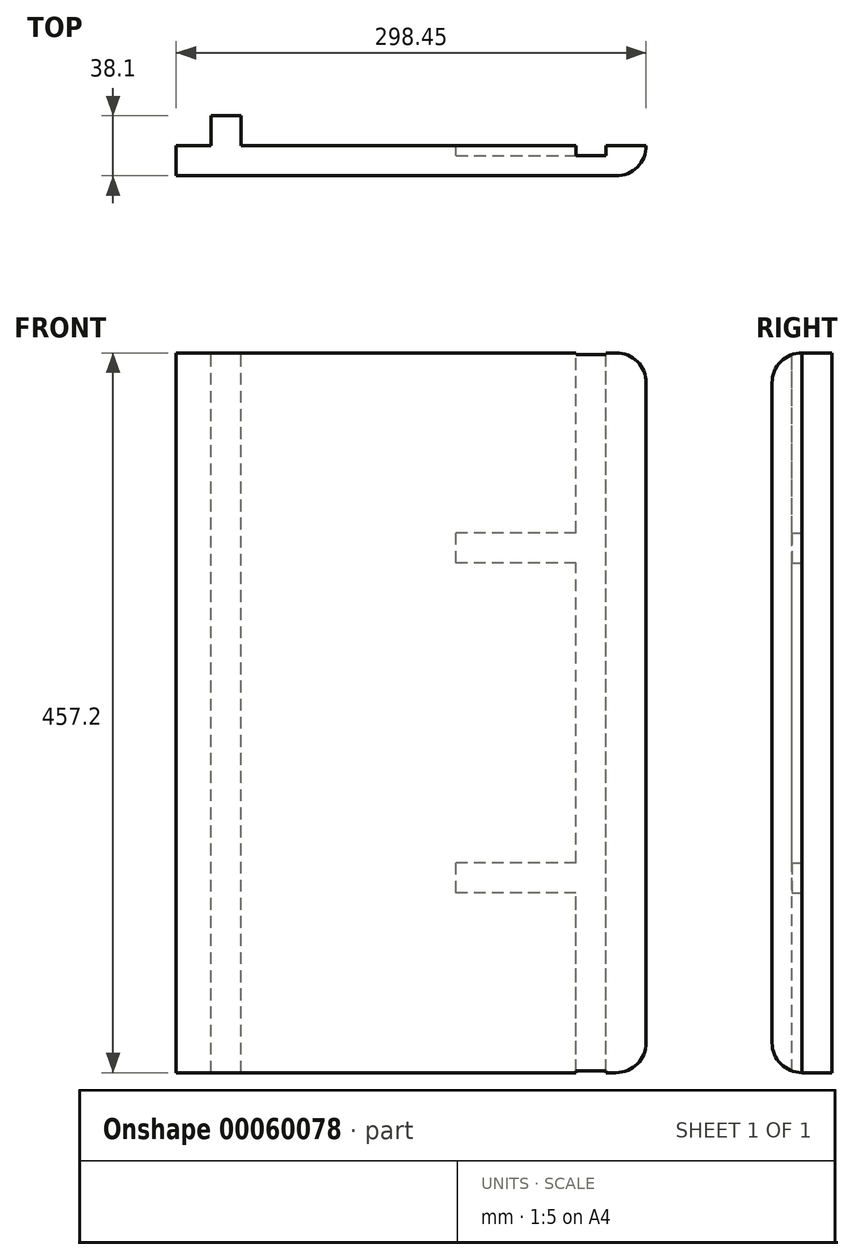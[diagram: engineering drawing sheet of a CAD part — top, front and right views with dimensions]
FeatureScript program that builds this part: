
annotation { "Feature Type Name" : "Feature", "Feature Type Description" : "" }
export const myFeature = defineFeature(function(context is Context, id is Id, definition is map)
    precondition{}
    {
        {
            var Q0;
            Q0=qCreatedBy(makeId("Front.planeOp"),FACE);
            var sketch = newSketch(context, id + "F0", { "sketchPlane" : qUnion([Q0])});
            skLineSegment(sketch, "E0.bottom", {"start": v(-149.23, -228.6) * mm, "end": v(149.22, -228.6) * mm});
            skLineSegment(sketch, "E0.top", {"start": v(-149.22, 228.6) * mm, "end": v(149.23, 228.6) * mm});
            skLineSegment(sketch, "E0.left", {"start": v(-149.23, -228.6) * mm, "end": v(-149.22, 228.6) * mm});
            skLineSegment(sketch, "E0.right", {"start": v(149.23, -228.6) * mm, "end": v(149.23, 228.6) * mm});
            skLineSegment(sketch, "E1", {"start": v(-149.22, 228.6) * mm, "end": v(149.23, -228.6) * mm, "construction": true});
            skSolve(sketch);
        }
        {
            var Q0;
            Q0=qSketchRegion(id+"F0",true);
            extrude(context, id + "F1", {"entities" : qUnion([Q0]), "oppositeDirection" : true, "depth" : 19.05 * mm});
        }
        {
            var Q0;
            Q0=makeQuery(id+"F1.opExtrude","CAP_FACE",FACE,{"disambiguationData":[OSD([sQuery(id+"F0.wireOp",EDGE,"E0.bottom"),sQuery(id+"F0.wireOp",EDGE,"E0.top"),sQuery(id+"F0.wireOp",EDGE,"E0.left"),sQuery(id+"F0.wireOp",EDGE,"E0.right")])],"isStart":false});
            var sketch = newSketch(context, id + "F3", { "sketchPlane" : qUnion([Q0])});
            skLineSegment(sketch, "E2.bottom", {"start": v(-123.82, -228.6) * mm, "end": v(-104.78, -228.6) * mm});
            skLineSegment(sketch, "E2.top", {"start": v(-123.83, 228.6) * mm, "end": v(-104.78, 228.6) * mm});
            skLineSegment(sketch, "E2.left", {"start": v(-123.82, -228.6) * mm, "end": v(-123.83, 228.6) * mm});
            skLineSegment(sketch, "E2.right", {"start": v(-104.78, -228.6) * mm, "end": v(-104.78, 228.6) * mm});
            skSolve(sketch);
        }
        {
            var Q0;
            Q0 = qSketchRegion(id + "F3", true);
            extrude(context, id + "F4", {"entities" : qUnion([Q0]), "operationType" : NewBodyOperationType.REMOVE, "oppositeDirection" : true, "depth" : 6.35 * mm});
        }
        {
            var Q0;
            Q0=makeQuery(id+"F1.opExtrude","CAP_EDGE",EDGE,{"disambiguationData":[OSD([sQuery(id+"F0.wireOp",EDGE,"E0.bottom")])],"isStart":true});
            var Q1;
            Q1=makeQuery(id+"F1.opExtrude","CAP_EDGE",EDGE,{"disambiguationData":[OSD([sQuery(id+"F0.wireOp",EDGE,"E0.right")])],"isStart":true});
            var Q2;
            Q2=makeQuery(id+"F1.opExtrude","CAP_EDGE",EDGE,{"disambiguationData":[OSD([sQuery(id+"F0.wireOp",EDGE,"E0.top")])],"isStart":true});
            var Q3;
            Q3=makeQuery(id+"F1.opExtrude","SWEPT_EDGE",EDGE,{"disambiguationData":[OSD([sQuery(id+"F0.wireOp",EDGE,"E0.bottom"),sQuery(id+"F0.wireOp",EDGE,"E0.right")])]});
            var Q4;
            Q4=makeQuery(id+"F1.opExtrude","SWEPT_EDGE",EDGE,{"disambiguationData":[OSD([sQuery(id+"F0.wireOp",EDGE,"E0.top"),sQuery(id+"F0.wireOp",EDGE,"E0.right")])]});
            fillet(context, id + "F5", {"entities" : qUnion([Q0, Q1, Q2, Q3, Q4]), "radius" : 19.05 * mm, "tangentPropagation" : true, "allowEdgeOverflow" : false});
        }
        {
            var Q0;
            {var subQ0=sQuery(id+"F0.wireOp",EDGE,"E0.bottom");var subQ1=sQuery(id+"F0.wireOp",EDGE,"E0.top");var subQ2=sQuery(id+"F0.wireOp",EDGE,"E0.left");Q0=makeQuery(id+"F4.boolean.opBoolean","SPLIT",FACE,{"disambiguationData":[TD([makeQuery(id+"F1.opExtrude","SWEPT_FACE",FACE,{"disambiguationData":[OSD([subQ2])]})])],"derivedFrom":makeQuery(id+"F1.opExtrude","CAP_FACE",FACE,{"disambiguationData":[OSD([subQ0,subQ1,subQ2,sQuery(id+"F0.wireOp",EDGE,"E0.right")])],"isStart":false})});}
            var sketch = newSketch(context, id + "F6", { "sketchPlane" : qUnion([Q0])});
            skLineSegment(sketch, "E3.bottom", {"start": v(127, -228.6) * mm, "end": v(107.95, -228.6) * mm});
            skLineSegment(sketch, "E3.top", {"start": v(127, 228.6) * mm, "end": v(107.95, 228.6) * mm});
            skLineSegment(sketch, "E3.left", {"start": v(127, -228.6) * mm, "end": v(127, 228.6) * mm});
            skLineSegment(sketch, "E3.right", {"start": v(107.95, -228.6) * mm, "end": v(107.95, 228.6) * mm});
            skSolve(sketch);
        }
        {
            var Q0;
            Q0 = qSketchRegion(id + "F6", true);
            extrude(context, id + "F7", {"entities" : qUnion([Q0]), "operationType" : NewBodyOperationType.ADD, "depth" : 19.05 * mm});
        }
        {
            var Q0;
            {var subQ0=sQuery(id+"F0.wireOp",EDGE,"E0.top");var subQ1=sQuery(id+"F0.wireOp",EDGE,"E0.bottom");var subQ2=makeQuery(id+"F4.opExtrude","SWEPT_FACE",FACE,{"disambiguationData":[OSD([sQuery(id+"F3.wireOp",EDGE,"E2.right")])]});var subQ3=sQuery(id+"F0.wireOp",EDGE,"E0.left");Q0=makeQuery(id+"F7.boolean.opBoolean","SPLIT",FACE,{"disambiguationData":[TD([makeQuery(id+"F4.boolean.opBoolean","COPY",FACE,{"derivedFrom":subQ2})])],"derivedFrom":makeQuery(id+"F4.boolean.opBoolean","SPLIT",FACE,{"disambiguationData":[TD([makeQuery(id+"F1.opExtrude","SWEPT_FACE",FACE,{"disambiguationData":[OSD([subQ3])]})])],"derivedFrom":makeQuery(id+"F1.opExtrude","CAP_FACE",FACE,{"disambiguationData":[OSD([subQ1,subQ0,subQ3,sQuery(id+"F0.wireOp",EDGE,"E0.right")])],"isStart":false})})});}
            var sketch = newSketch(context, id + "F8", { "sketchPlane" : qUnion([Q0])});
            skLineSegment(sketch, "E4.bottom", {"start": v(-104.78, 95.25) * mm, "end": v(-28.58, 95.25) * mm});
            skLineSegment(sketch, "E4.top", {"start": v(-104.78, 114.3) * mm, "end": v(-28.58, 114.3) * mm});
            skLineSegment(sketch, "E4.left", {"start": v(-104.78, 95.25) * mm, "end": v(-104.78, 114.3) * mm});
            skLineSegment(sketch, "E4.right", {"start": v(-28.58, 95.25) * mm, "end": v(-28.58, 114.3) * mm});
            skLineSegment(sketch, "E5.bottom", {"start": v(-104.78, -114.3) * mm, "end": v(-28.58, -114.3) * mm});
            skLineSegment(sketch, "E5.top", {"start": v(-104.78, -95.25) * mm, "end": v(-28.58, -95.25) * mm});
            skLineSegment(sketch, "E5.left", {"start": v(-104.78, -114.3) * mm, "end": v(-104.78, -95.25) * mm});
            skLineSegment(sketch, "E5.right", {"start": v(-28.58, -114.3) * mm, "end": v(-28.58, -95.25) * mm});
            skSolve(sketch);
        }
        {
            var Q0;
            Q0 = qSketchRegion(id + "F8", true);
            var Q1;
            Q1=makeQuery(id+"F4.boolean.opBoolean","COPY",FACE,{"derivedFrom":makeQuery(id+"F4.opExtrude","CAP_FACE",FACE,{"disambiguationData":[OSD([sQuery(id+"F3.wireOp",EDGE,"E2.bottom"),sQuery(id+"F3.wireOp",EDGE,"E2.top"),sQuery(id+"F3.wireOp",EDGE,"E2.left"),sQuery(id+"F3.wireOp",EDGE,"E2.right")])],"isStart":false})});
            extrude(context, id + "F9", {"entities" : qUnion([Q0]), "operationType" : NewBodyOperationType.REMOVE, "endBound" : BoundingType.UP_TO_SURFACE, "oppositeDirection" : true, "endBoundEntityFace" : qUnion([Q1]), "depth" : 25.4 * mm});
        }
    });
